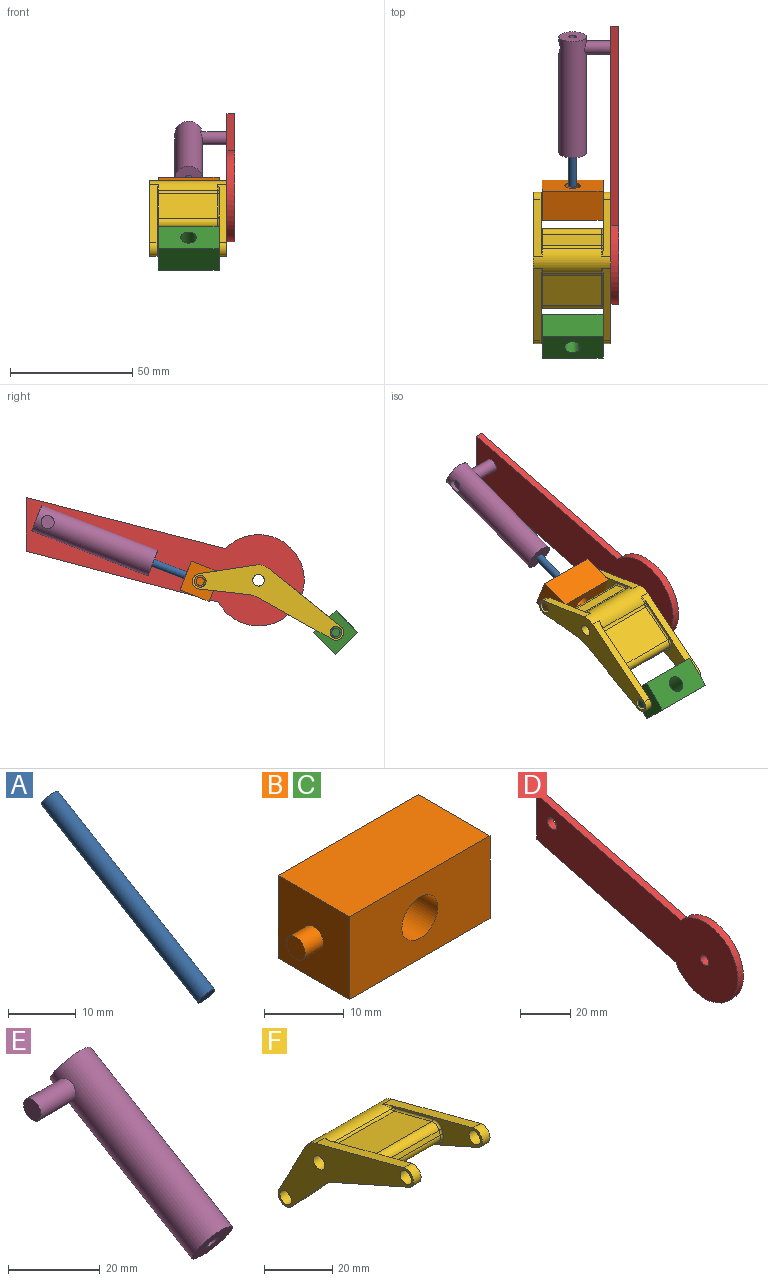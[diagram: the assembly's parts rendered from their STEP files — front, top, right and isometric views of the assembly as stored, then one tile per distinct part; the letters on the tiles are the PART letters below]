
ASSEMBLY  parts=6 mates=6
PART A: 3 faces, bbox 3.2x34.3x22.2 mm
  f0: cylinder r=1.59mm len=34.35mm, axis (0,-0.86,-0.51), area 380mm2, adj f1,f2
  f1: plane 3.18x2.73mm, normal (0,0.86,0.51), area 7.9mm2, adj f0
  f2: plane 3.18x2.73mm, normal (0,-0.86,-0.51), area 7.9mm2, adj f0
PART B: 11 faces, bbox 31.3x12.7x12.7 mm
  f0: cylinder r=1.68mm len=3.36mm, axis (-1,0,0), area 34.1mm2, adj f1,f6
  f1: plane 3.36x3.36mm, normal (-1,0,0), area 8.9mm2, adj f0
  f2: plane 24.89x12.7mm, normal (0,0,1), area 316.1mm2, adj f3,f5,f6,f9
  f3: plane 24.89x12.7mm, normal (0,-1,0), area 284.5mm2, adj f2,f4,f6,f9,f10
  f4: plane 24.89x12.7mm, normal (0,0,-1), area 316.1mm2, adj f3,f5,f6,f9
  f5: plane 24.89x12.7mm, normal (0,1,0), area 284.5mm2, adj f2,f4,f6,f9,f10
  f6: plane 12.7x12.7mm, normal (-1,0,0), area 152.4mm2, adj f0,f2,f3,f4,f5
  f7: cylinder r=1.68mm len=3.36mm, axis (1,0,0), area 34.1mm2, adj f8,f9
  f8: plane 3.36x3.36mm, normal (1,0,0), area 8.9mm2, adj f7
  f9: plane 12.7x12.7mm, normal (1,0,0), area 152.4mm2, adj f2,f3,f4,f5,f7
  f10: cylinder r=3.17mm len=12.7mm, axis (0,-1,0), area 253.4mm2, adj f3,f5
PART C: same geometry as B
PART D: 8 faces, bbox 3.2x113.6x52.4 mm
  f0: cylinder r=18.65mm len=37.3mm, axis (-1,0,0), area 297.1mm2, adj f2,f3,f4,f5
  f1: cylinder r=2.38mm len=4.76mm, axis (-1,0,0), area 47.5mm2, adj f2,f3
  f2: plane 113.56x52.43mm, normal (1,0,0), area 2779.6mm2, adj f0,f1,f4,f5,f6,f7
  f3: plane 113.56x52.43mm, normal (-1,0,0), area 2779.6mm2, adj f0,f1,f4,f5,f6,f7
  f4: plane 81.46x20.86mm, normal (0,-0.25,0.97), area 267mm2, adj f0,f2,f3,f6
  f5: plane 78.55x20.81mm, normal (0,0.26,-0.97), area 258mm2, adj f0,f2,f3,f6
  f6: plane 21.91x3.18mm, normal (0,1,0), area 69.6mm2, adj f2,f3,f4,f5
  f7: cylinder r=2.7mm len=5.4mm, axis (1,0,0), area 53.8mm2, adj f2,f3
PART E: 11 faces, bbox 21.5x49.4x35.6 mm
  f0: cylinder r=1.59mm len=4.03mm, axis (0,-0.86,-0.51), area 22.8mm2, adj f3,f10
  f1: cylinder r=1.59mm len=39.32mm, axis (0,-0.86,-0.51), area 435.1mm2, adj f4,f9
  f2: cylinder r=5.6mm len=49.36mm, axis (0,-0.86,-0.51), area 1740mm2, adj f3,f4,f5,f8
  f3: plane 11.2x9.62mm, normal (0,0.86,0.51), area 90.6mm2, adj f0,f2
  f4: plane 11.2x9.62mm, normal (0,-0.86,-0.51), area 90.6mm2, adj f1,f2
  f5: cylinder r=2.7mm len=5.4mm, axis (1,0,0), area 35.3mm2, adj f2,f6
  f6: plane 5.4x5.4mm, normal (1,0,0), area 22.9mm2, adj f5
  f7: plane 5.4x5.4mm, normal (-1,0,0), area 22.9mm2, adj f8
  f8: cylinder r=2.7mm len=10.97mm, axis (-1,0,0), area 180mm2, adj f2,f7
  f9: cylinder r=2.7mm len=3.18mm, axis (-1,0,0), area 8.3mm2, adj f1
  f10: cylinder r=2.7mm len=3.18mm, axis (-1,0,0), area 8.3mm2, adj f0
PART F: 79 faces, bbox 31.9x56.2x38.6 mm
  f0: plane 22.97x19.51mm, normal (-1,0,0), area 99.2mm2, adj f3,f4,f5,f10,f11,f39,f40,f41
  f1: cylinder r=3.17mm len=6.08mm, axis (-1,0,0), area 30mm2, adj f2,f7,f8,f9
  f2: plane 31.03x13.82mm, normal (0,-0.41,-0.91), area 107.8mm2, adj f1,f8,f9,f10
  f3: plane 14.59x13.58mm, normal (0,-0.73,-0.68), area 63.3mm2, adj f0,f4,f8,f10
  f4: cylinder r=3.17mm len=5.5mm, axis (-1,0,0), area 29mm2, adj f0,f3,f5,f8
  f5: plane 21.01x11.17mm, normal (0,0.88,0.47), area 75.7mm2, adj f0,f4,f6,f8,f47
  f6: cylinder r=6.35mm len=31.75mm, axis (-1,0,0), area 332.7mm2, adj f5,f7,f8,f21,f28,f29,f47,f53
  f7: plane 36.85x9.76mm, normal (0,0.25,0.97), area 121.3mm2, adj f1,f6,f8,f9,f29
  f8: plane 56.12x38.44mm, normal (1,0,0), area 567.8mm2, adj f1,f2,f3,f4,f5,f6,f7,f10
  f9: plane 37.89x20.26mm, normal (-1,0,0), area 132.8mm2, adj f1,f2,f7,f10,f13,f29,f30,f31
  f10: cylinder r=12.7mm len=4.13mm, axis (1,0,0), area 16.2mm2, adj f0,f2,f3,f8,f9,f38
  f11: cylinder r=2.38mm len=4.76mm, axis (1,0,0), area 47.5mm2, adj f0,f8
  f12: cylinder r=2.38mm len=31.75mm, axis (1,0,0), area 475mm2, adj f8,f55
  f13: cylinder r=2.38mm len=4.76mm, axis (1,0,0), area 47.5mm2, adj f8,f9
  f14: plane 24.13x4.18mm, normal (0,0.88,0.47), area 114.1mm2, adj f21,f22,f45,f76
  f15: plane 24.13x2.03mm, normal (0,0.58,-0.81), area 60.2mm2, adj f22,f23,f43,f74
  f16: plane 24.13x3.36mm, normal (0,-0.73,-0.68), area 110.7mm2, adj f23,f24,f41,f72
  f17: cylinder r=6.35mm len=24.13mm, axis (1,0,0), area 112.7mm2, adj f24,f25,f37,f38,f39,f68,f69,f70
  f18: plane 24.13x14.51mm, normal (0,-0.41,-0.91), area 383.2mm2, adj f25,f26,f35,f66
  f19: plane 24.13x1.45mm, normal (0,-0.94,0.33), area 37.1mm2, adj f26,f27,f33,f64
  f20: plane 24.13x15.6mm, normal (0,0.25,0.97), area 389.1mm2, adj f27,f28,f31,f62
  f21: cylinder r=2.54mm len=24.13mm, axis (-1,0,0), area 33.2mm2, adj f6,f14,f46,f77
  f22: cylinder r=2.54mm len=24.13mm, axis (1,0,0), area 88.1mm2, adj f14,f15,f44,f75
  f23: cylinder r=2.54mm len=24.13mm, axis (1,0,0), area 88.3mm2, adj f15,f16,f42,f73
  f24: cylinder r=2.54mm len=24.13mm, axis (1,0,0), area 34.5mm2, adj f16,f17,f40,f71
  f25: cylinder r=2.54mm len=24.13mm, axis (1,0,0), area 35.3mm2, adj f17,f18,f36,f67
  f26: cylinder r=2.54mm len=24.13mm, axis (1,0,0), area 91.4mm2, adj f18,f19,f34,f65
  f27: cylinder r=2.54mm len=24.13mm, axis (1,0,0), area 91.2mm2, adj f19,f20,f32,f63
  f28: cylinder r=2.54mm len=24.13mm, axis (-1,0,0), area 33.2mm2, adj f6,f20,f30,f61
  f29: torus R=6.99mm, axis (1,0,0), area 2.1mm2, adj f6,f7,f9,f30
  f30: torus R=1.91mm, axis (1,0,0), area 1.2mm2, adj f9,f28,f29,f31
  f31: cylinder r=0.64mm len=15.76mm, axis (0,-0.97,0.25), area 16.1mm2, adj f9,f20,f30,f32
  f32: torus R=3.17mm, axis (1,0,0), area 4.1mm2, adj f9,f27,f31,f33
  f33: cylinder r=0.64mm len=1.66mm, axis (0,-0.33,-0.94), area 1.5mm2, adj f9,f19,f32,f34
  f34: torus R=3.17mm, axis (1,0,0), area 4.1mm2, adj f9,f26,f33,f35
  f35: cylinder r=0.64mm len=14.77mm, axis (0,0.91,-0.41), area 15.8mm2, adj f9,f18,f34,f36
  f36: torus R=1.91mm, axis (1,0,0), area 1.3mm2, adj f9,f25,f35,f37
  f37: torus R=6.99mm, axis (1,0,0), area 0.7mm2, adj f9,f17,f36,f38
  f38: bspline ~3.65x2.91mm, area 2.5mm2, adj f10,f17,f37,f39
  f39: torus R=6.99mm, axis (1,0,0), area 0.7mm2, adj f0,f17,f38,f40
  f40: torus R=1.91mm, axis (1,0,0), area 1.3mm2, adj f0,f24,f39,f41
  f41: cylinder r=0.64mm len=3.79mm, axis (0,0.68,-0.73), area 4.6mm2, adj f0,f16,f40,f42
  f42: torus R=3.17mm, axis (1,0,0), area 4mm2, adj f0,f23,f41,f43
  f43: cylinder r=0.64mm len=2.4mm, axis (0,0.81,0.58), area 2.5mm2, adj f0,f15,f42,f44
  f44: torus R=3.17mm, axis (1,0,0), area 4mm2, adj f0,f22,f43,f45
  f45: cylinder r=0.64mm len=4.48mm, axis (0,-0.47,0.88), area 4.7mm2, adj f0,f14,f44,f46
  f46: torus R=1.91mm, axis (1,0,0), area 1.2mm2, adj f0,f21,f45,f47
  f47: torus R=6.99mm, axis (1,0,0), area 2.1mm2, adj f0,f5,f6,f46
  f48: plane 22.97x19.51mm, normal (1,0,0), area 99.2mm2, adj f51,f52,f53,f57,f58,f70,f71,f72
  f49: cylinder r=3.17mm len=6.08mm, axis (1,0,0), area 30mm2, adj f50,f54,f55,f56
  f50: plane 31.03x13.82mm, normal (0,-0.41,-0.91), area 107.8mm2, adj f49,f55,f56,f57
  f51: plane 14.59x13.58mm, normal (0,-0.73,-0.68), area 63.3mm2, adj f48,f52,f55,f57
  f52: cylinder r=3.17mm len=5.5mm, axis (1,0,0), area 29mm2, adj f48,f51,f53,f55
  f53: plane 21.01x11.17mm, normal (0,0.88,0.47), area 75.7mm2, adj f6,f48,f52,f55,f78
  f54: plane 36.85x9.76mm, normal (0,0.25,0.97), area 121.3mm2, adj f6,f49,f55,f56,f60
  f55: plane 56.12x38.44mm, normal (-1,0,0), area 567.8mm2, adj f6,f12,f49,f50,f51,f52,f53,f54
  f56: plane 37.89x20.26mm, normal (1,0,0), area 132.8mm2, adj f49,f50,f54,f57,f59,f60,f61,f62
  f57: cylinder r=12.7mm len=4.13mm, axis (-1,0,0), area 16.2mm2, adj f48,f50,f51,f55,f56,f69
  f58: cylinder r=2.38mm len=4.76mm, axis (-1,0,0), area 47.5mm2, adj f48,f55
  f59: cylinder r=2.38mm len=4.76mm, axis (-1,0,0), area 47.5mm2, adj f55,f56
  f60: torus R=6.99mm, axis (-1,0,0), area 2.1mm2, adj f6,f54,f56,f61
  f61: torus R=1.91mm, axis (-1,0,0), area 1.2mm2, adj f28,f56,f60,f62
  f62: cylinder r=0.64mm len=15.76mm, axis (0,-0.97,0.25), area 16.1mm2, adj f20,f56,f61,f63
  f63: torus R=3.17mm, axis (-1,0,0), area 4.1mm2, adj f27,f56,f62,f64
  f64: cylinder r=0.64mm len=1.66mm, axis (0,-0.33,-0.94), area 1.5mm2, adj f19,f56,f63,f65
  f65: torus R=3.17mm, axis (-1,0,0), area 4.1mm2, adj f26,f56,f64,f66
  f66: cylinder r=0.64mm len=14.77mm, axis (0,0.91,-0.41), area 15.8mm2, adj f18,f56,f65,f67
  f67: torus R=1.91mm, axis (-1,0,0), area 1.3mm2, adj f25,f56,f66,f68
  f68: torus R=6.99mm, axis (-1,0,0), area 0.7mm2, adj f17,f56,f67,f69
  f69: bspline ~3.65x2.91mm, area 2.5mm2, adj f17,f57,f68,f70
  f70: torus R=6.99mm, axis (-1,0,0), area 0.7mm2, adj f17,f48,f69,f71
  f71: torus R=1.91mm, axis (-1,0,0), area 1.3mm2, adj f24,f48,f70,f72
  f72: cylinder r=0.64mm len=3.79mm, axis (0,0.68,-0.73), area 4.6mm2, adj f16,f48,f71,f73
  f73: torus R=3.17mm, axis (-1,0,0), area 4mm2, adj f23,f48,f72,f74
  f74: cylinder r=0.64mm len=2.4mm, axis (0,0.81,0.58), area 2.5mm2, adj f15,f48,f73,f75
  f75: torus R=3.17mm, axis (-1,0,0), area 4mm2, adj f22,f48,f74,f76
  f76: cylinder r=0.64mm len=4.48mm, axis (0,-0.47,0.88), area 4.7mm2, adj f14,f48,f75,f77
  f77: torus R=1.91mm, axis (-1,0,0), area 1.2mm2, adj f21,f48,f76,f78
  f78: torus R=6.99mm, axis (-1,0,0), area 2.1mm2, adj f6,f48,f53,f77
PLACE A rot(axis=(-1,0,0),9.6deg) t=(-2.97,2.41,35.18)mm
PLACE B rot(axis=(1,0,0),21.2deg) t=(9.93,44.98,12.58)mm
PLACE C rot(axis=(-1,0,0),44.7deg) t=(9.93,-31.91,-43.74)mm
PLACE D t=(9.52,-16.93,11.86)mm fixed
PLACE E rot(axis=(0,-0.9,-0.44),180deg) t=(-2.97,-2.53,-17.68)mm
PLACE F rot(axis=(1,0,0),53.5deg) t=(9.52,-16.93,11.86)mm
MATE cylindrical E.f5 <-> D.f7  axis (1,0,0) through (7.38,69.19,35.59)mm
MATE revolute C.f0 <-> F.f1  axis (1,0,0) through (12.7,-48.52,-9.45)mm
MATE slider E.f0 <-> A.f0  axis (0,-0.93,-0.36) through (-2.97,26.24,18.94)mm
MATE revolute D.f1 <-> F.f12  axis (-1,0,0) through (12.7,-16.93,11.86)mm
MATE fastened A.f0 <-> B.f10  axis (0,-0.93,-0.36) through (-2.97,12.81,13.74)mm
MATE revolute F.f4 <-> B.f0  axis (1,0,0) through (12.7,6.89,11.44)mm
